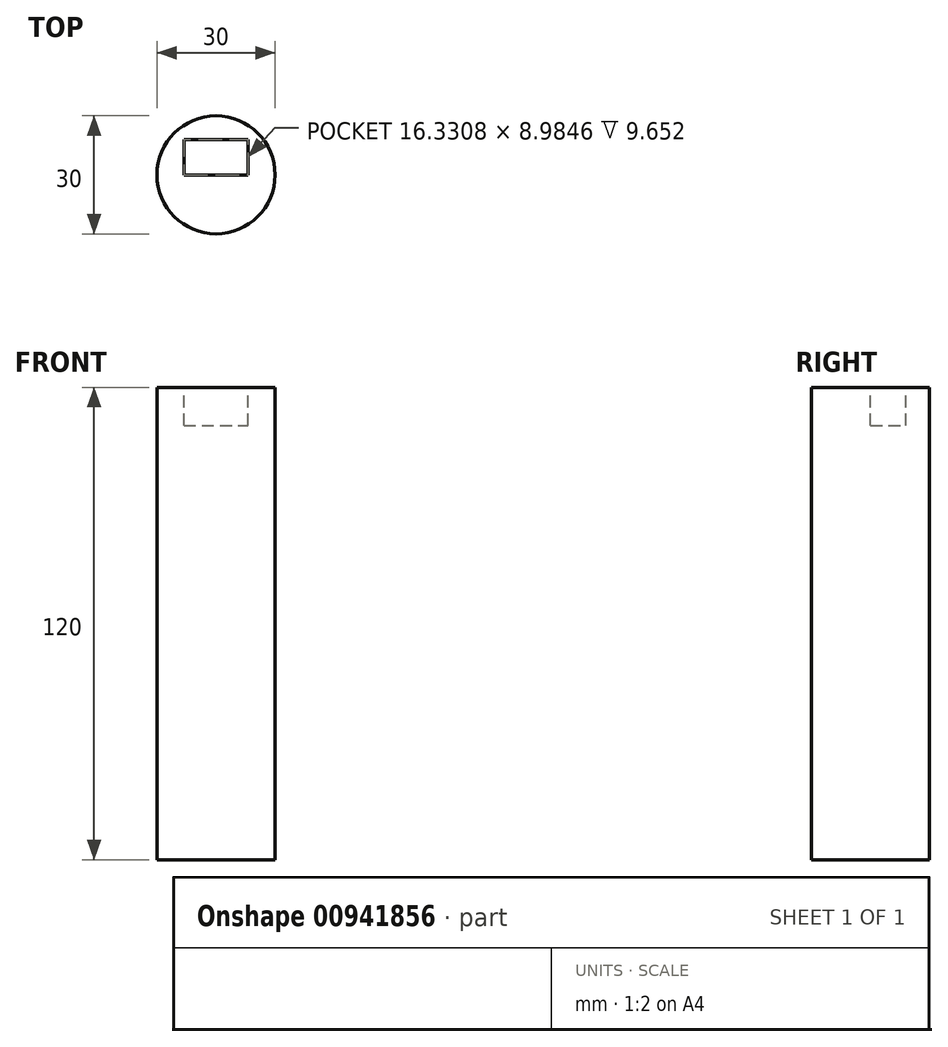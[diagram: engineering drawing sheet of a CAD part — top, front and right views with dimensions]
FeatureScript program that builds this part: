
annotation { "Feature Type Name" : "Feature", "Feature Type Description" : "" }
export const myFeature = defineFeature(function(context is Context, id is Id, definition is map)
    precondition{}
    {
        {
            var Q0;
            Q0=qCreatedBy(makeId("Top.planeOp"),FACE);
            var sketch = newSketch(context, id + "F0", { "sketchPlane" : qUnion([Q0])});
            skCircle(sketch, "E0", {"center": v(0, 0) * mm, "radius": 15 * mm});
            skSolve(sketch);
        }
        {
            var Q0;
            Q0=makeQuery(id+"F0.imprint","IMPRINT",FACE,{"disambiguationData":[TD([[makeQuery(id+"F0.imprint","IMPRINT",EDGE,{"derivedFrom":sQuery(id+"F0.wireOp",EDGE,"E0")}),1.0]])]});
            extrude(context, id + "F1", {"entities" : qUnion([Q0]), "oppositeDirection" : true, "depth" : 120 * mm, "offsetDistance" : 25.4 * mm});
        }
        {
            var Q0;
            Q0=qCreatedBy(makeId("Top.planeOp"),FACE);
            var sketch = newSketch(context, id + "F2", { "sketchPlane" : qUnion([Q0])});
            skLineSegment(sketch, "E1.bottom", {"start": v(-8.17, 0) * mm, "end": v(8.17, 0) * mm});
            skLineSegment(sketch, "E1.top", {"start": v(-8.17, 8.98) * mm, "end": v(8.17, 8.98) * mm});
            skLineSegment(sketch, "E1.left", {"start": v(-8.17, 0) * mm, "end": v(-8.17, 8.98) * mm});
            skLineSegment(sketch, "E1.right", {"start": v(8.17, 0) * mm, "end": v(8.17, 8.98) * mm});
            skSolve(sketch);
        }
        {
            var Q0;
            Q0=makeQuery(id+"F2.imprint","IMPRINT",FACE,{"disambiguationData":[TD([[makeQuery(id+"F2.imprint","IMPRINT",EDGE,{"derivedFrom":sQuery(id+"F2.wireOp",EDGE,"E1.bottom")}),1.0]])]});
            extrude(context, id + "F3", {"entities" : qUnion([Q0]), "operationType" : NewBodyOperationType.REMOVE, "oppositeDirection" : true, "depth" : 9.65 * mm, "offsetDistance" : 25.4 * mm});
        }
    });
